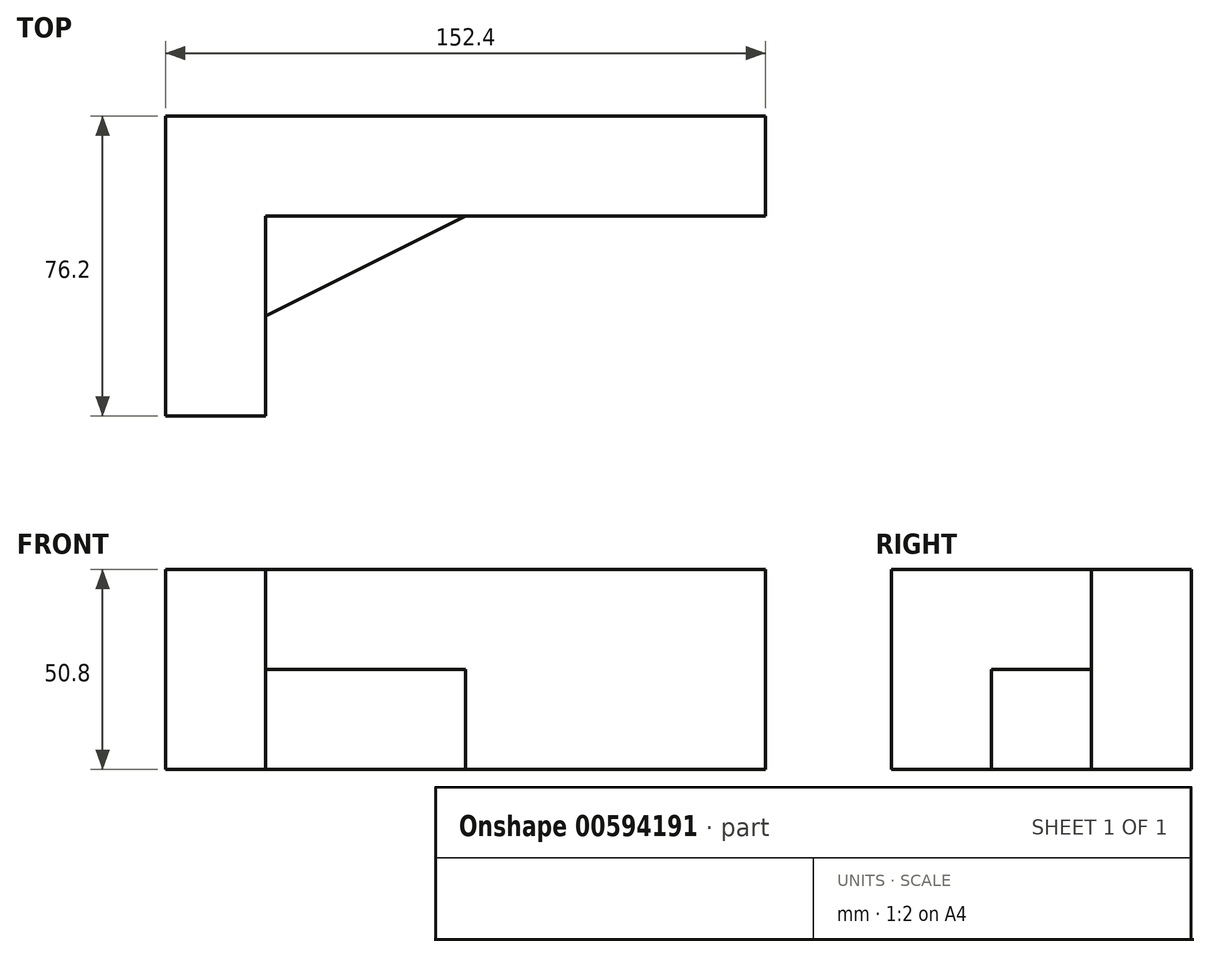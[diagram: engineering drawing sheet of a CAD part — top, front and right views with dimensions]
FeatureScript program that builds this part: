
annotation { "Feature Type Name" : "Feature", "Feature Type Description" : "" }
export const myFeature = defineFeature(function(context is Context, id is Id, definition is map)
    precondition{}
    {
        {
            var Q0;
            Q0=qCreatedBy(makeId("Top.planeOp"),FACE);
            var sketch = newSketch(context, id + "F0", { "sketchPlane" : qUnion([Q0])});
            skLineSegment(sketch, "E0.bottom", {"start": v(0, 0) * mm, "end": v(152.4, 0) * mm});
            skLineSegment(sketch, "E0.top", {"start": v(0, 76.2) * mm, "end": v(152.4, 76.2) * mm});
            skLineSegment(sketch, "E0.left", {"start": v(0, 0) * mm, "end": v(0, 76.2) * mm});
            skLineSegment(sketch, "E0.right", {"start": v(152.4, 0) * mm, "end": v(152.4, 76.2) * mm});
            skSolve(sketch);
        }
        {
            var Q0;
            Q0=makeQuery(id+"F0.imprint","IMPRINT",FACE,{"disambiguationData":[TD([[makeQuery(id+"F0.imprint","IMPRINT",EDGE,{"derivedFrom":sQuery(id+"F0.wireOp",EDGE,"E0.bottom")}),1.0]])]});
            extrude(context, id + "F1", {"entities" : qUnion([Q0]), "depth" : 50.8 * mm, "offsetDistance" : 25.4 * mm});
        }
        {
            var Q0;
            Q0=makeQuery(id+"F1.opExtrude","CAP_FACE",FACE,{"disambiguationData":[OSD([sQuery(id+"F0.wireOp",EDGE,"E0.bottom"),sQuery(id+"F0.wireOp",EDGE,"E0.top"),sQuery(id+"F0.wireOp",EDGE,"E0.left"),sQuery(id+"F0.wireOp",EDGE,"E0.right")])],"isStart":false});
            var sketch = newSketch(context, id + "F2", { "sketchPlane" : qUnion([Q0])});
            skLineSegment(sketch, "E1", {"start": v(0, 0) * mm, "end": v(25.4, 0) * mm});
            skLineSegment(sketch, "E2", {"start": v(25.4, 0) * mm, "end": v(25.4, 25.4) * mm});
            skLineSegment(sketch, "E3", {"start": v(76.2, 50.8) * mm, "end": v(152.4, 50.8) * mm});
            skLineSegment(sketch, "E4", {"start": v(152.4, 50.8) * mm, "end": v(152.4, 76.2) * mm});
            skLineSegment(sketch, "E5", {"start": v(152.4, 76.2) * mm, "end": v(0, 76.2) * mm});
            skLineSegment(sketch, "E6", {"start": v(0, 76.2) * mm, "end": v(0, 0) * mm});
            skLineSegment(sketch, "E7", {"start": v(25.4, 25.4) * mm, "end": v(76.2, 50.8) * mm});
            skLineSegment(sketch, "E8", {"start": v(25.4, 50.8) * mm, "end": v(76.2, 50.8) * mm});
            skLineSegment(sketch, "E9", {"start": v(25.4, 50.8) * mm, "end": v(25.4, 25.4) * mm});
            skSolve(sketch);
        }
        {
            var Q0;
            {var subQ3=sQuery(id+"F2.wireOp",EDGE,"E2");Q0=makeQuery(id+"F2.imprint","IMPRINT",FACE,{"disambiguationData":[TD([[makeQuery(id+"F2.imprint","IMPRINT",EDGE,{"derivedFrom":subQ3}),-1.0]])]});}
            extrude(context, id + "F3", {"entities" : qUnion([Q0]), "operationType" : NewBodyOperationType.REMOVE, "oppositeDirection" : true, "depth" : 50.8 * mm, "offsetDistance" : 25.4 * mm});
        }
        {
            var Q0;
            Q0=makeQuery(id+"F1.opExtrude","CAP_FACE",FACE,{"disambiguationData":[OSD([sQuery(id+"F0.wireOp",EDGE,"E0.bottom"),sQuery(id+"F0.wireOp",EDGE,"E0.top"),sQuery(id+"F0.wireOp",EDGE,"E0.left"),sQuery(id+"F0.wireOp",EDGE,"E0.right")])],"isStart":false});
            var sketch = newSketch(context, id + "F4", { "sketchPlane" : qUnion([Q0])});
            skLineSegment(sketch, "E10", {"start": v(76.2, 50.8) * mm, "end": v(25.4, 50.8) * mm});
            skLineSegment(sketch, "E11", {"start": v(25.4, 25.4) * mm, "end": v(25.4, 50.8) * mm});
            skSolve(sketch);
        }
        {
            var Q0;
            Q0=makeQuery(id+"F4.imprint","IMPRINT",FACE,{"disambiguationData":[TD([[makeQuery(id+"F4.imprint","IMPRINT",EDGE,{"derivedFrom":sQuery(id+"F4.wireOp",EDGE,"E10")}),1.0]])]});
            extrude(context, id + "F5", {"entities" : qUnion([Q0]), "operationType" : NewBodyOperationType.REMOVE, "oppositeDirection" : true, "depth" : 25.4 * mm, "offsetDistance" : 25.4 * mm});
        }
    });
